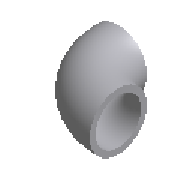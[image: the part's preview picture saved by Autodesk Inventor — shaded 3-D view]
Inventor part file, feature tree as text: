
AUTODESK INVENTOR PART (.ipt)
format: ipt  version: 2023.2 (Build 272271030, 271C)  size: 192,512 bytes
history: native  units: mm (DEFAULTED — no unit token found)
features: other x4, sketch x2, sweep x1
ambient origin geometry x8: Origin, YZ Plane, XZ Plane, XY Plane, X Axis, Y Axis, Z Axis, Center Point
bodies: Solid1 (feature_tree)
feature tree (7):
  sweep  "Sweep1"
  other  "Work Point1"
  other  "Work Axis1"
  other  "Work Point2"
  other  "Work Axis2"
  sketch  "Sketch1"  dims[d0=254.2mm d1=267.4mm]
  sketch  "Sketch2"  dims[d2=254.0mm d3=90.0deg d4=254.0mm d5=0.0mm d6=0.0mm]
